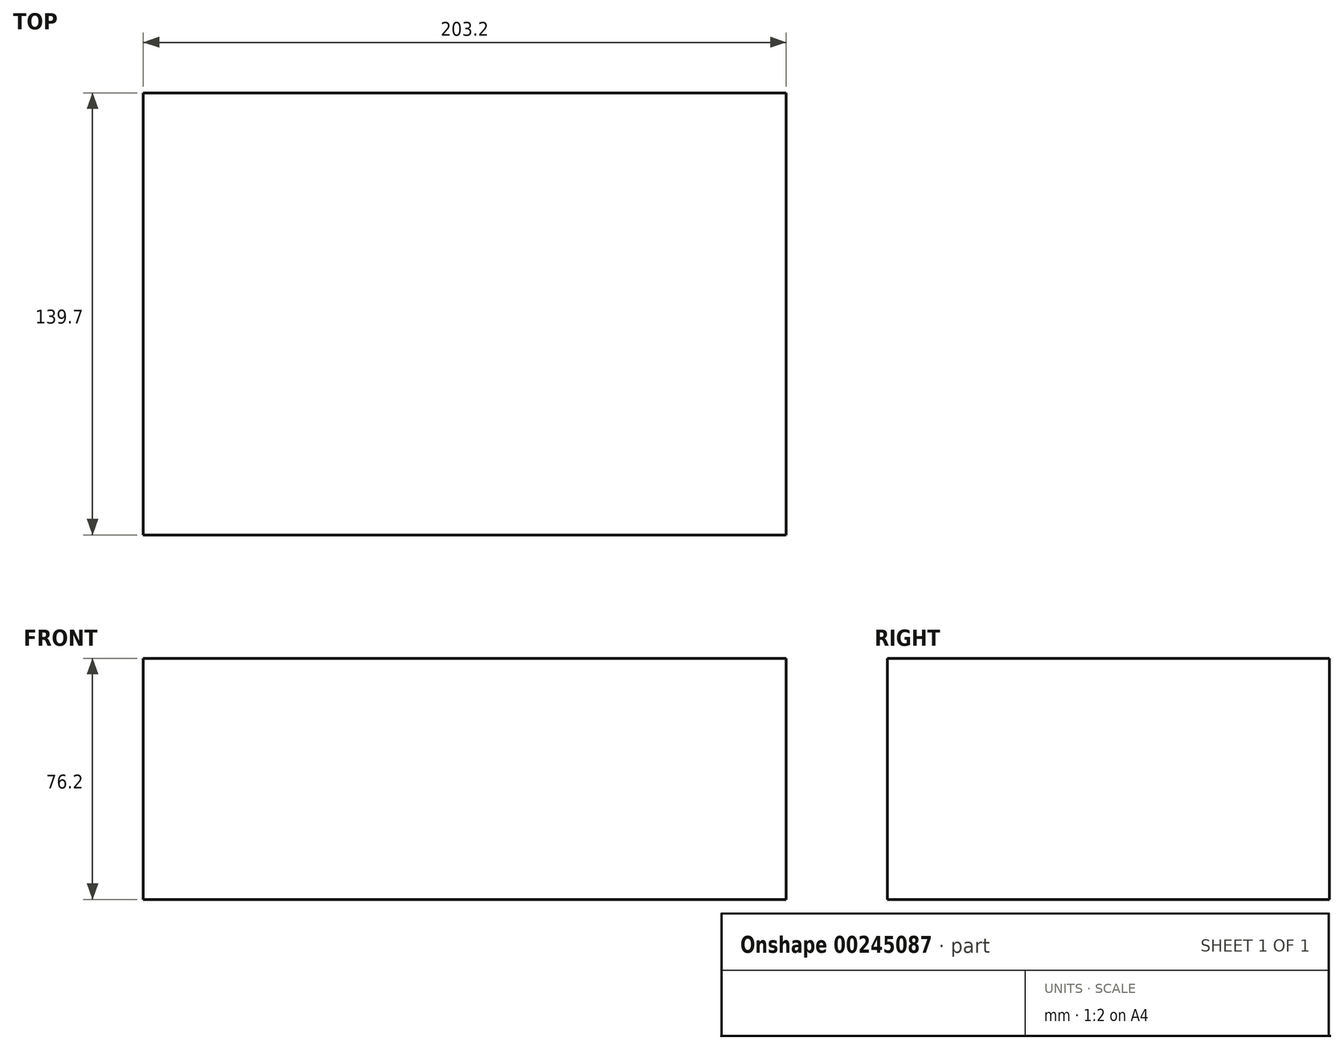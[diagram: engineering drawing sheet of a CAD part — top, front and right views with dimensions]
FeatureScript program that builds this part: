
annotation { "Feature Type Name" : "Feature", "Feature Type Description" : "" }
export const myFeature = defineFeature(function(context is Context, id is Id, definition is map)
    precondition{}
    {
        {
            var Q0;
            Q0=qCreatedBy(makeId("Top.planeOp"),FACE);
            var sketch = newSketch(context, id + "F0", { "sketchPlane" : qUnion([Q0])});
            skLineSegment(sketch, "E0.bottom", {"start": v(-101.6, 69.85) * mm, "end": v(101.6, 69.85) * mm});
            skLineSegment(sketch, "E0.top", {"start": v(-101.6, -69.85) * mm, "end": v(101.6, -69.85) * mm});
            skLineSegment(sketch, "E0.left", {"start": v(-101.6, 69.85) * mm, "end": v(-101.6, -69.85) * mm});
            skLineSegment(sketch, "E0.right", {"start": v(101.6, 69.85) * mm, "end": v(101.6, -69.85) * mm});
            skPoint(sketch, "E0.middle", {"position": v(0, 0) * mm});
            skSolve(sketch);
        }
        {
            var Q0;
            Q0=makeQuery(id+"F0.imprint","IMPRINT",FACE,{"disambiguationData":[TD([[makeQuery(id+"F0.imprint","IMPRINT",EDGE,{"derivedFrom":sQuery(id+"F0.wireOp",EDGE,"E0.bottom")}),-1.0]])]});
            extrude(context, id + "F1", {"entities" : qUnion([Q0]), "depth" : 76.2 * mm});
        }
    });
